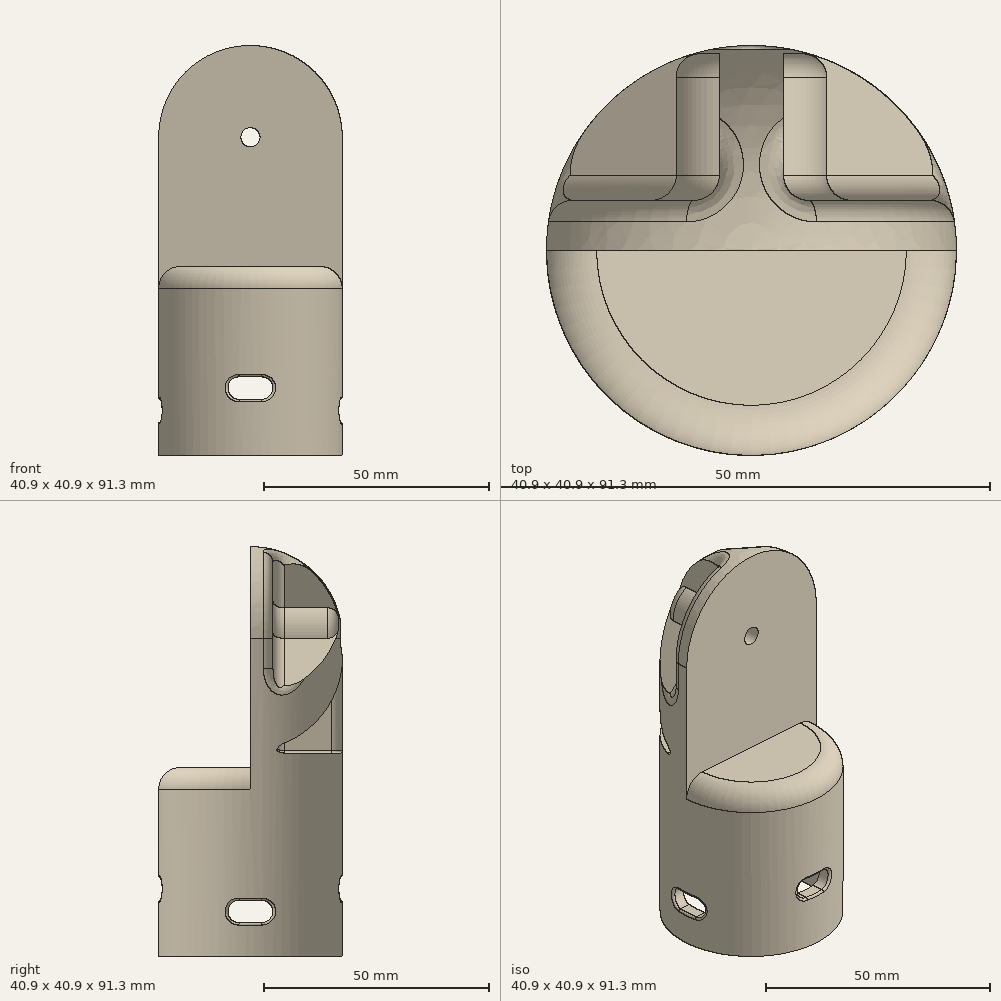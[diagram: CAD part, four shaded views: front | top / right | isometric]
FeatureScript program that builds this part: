
annotation { "Feature Type Name" : "Feature", "Feature Type Description" : "" }
export const myFeature = defineFeature(function(context is Context, id is Id, definition is map)
    precondition{}
    {
        {
            var Q0;
            Q0=qCreatedBy(makeId("Front.planeOp"),FACE);
            var sketch = newSketch(context, id + "F0", { "sketchPlane" : qUnion([Q0])});
            skLineSegment(sketch, "E0", {"start": v(17.25, 0) * mm, "end": v(17.25, 33.1) * mm});
            skLineSegment(sketch, "E1", {"start": v(12.25, 38.1) * mm, "end": v(0, 38.1) * mm});
            skLineSegment(sketch, "E2", {"start": v(0, 38.1) * mm, "end": v(0, 41.3) * mm});
            skLineSegment(sketch, "E3", {"start": v(0, 41.3) * mm, "end": v(20.45, 41.3) * mm, "construction": true});
            skLineSegment(sketch, "E4", {"start": v(20.45, 41.3) * mm, "end": v(20.45, 0) * mm});
            skLineSegment(sketch, "E5", {"start": v(20.45, 0) * mm, "end": v(17.25, 0) * mm});
            skPoint(sketch, "E6.visualSharp", {"position": v(17.25, 38.1) * mm});
            skArc(sketch, "E6.filletArc", {"start": v(17.25, 33.1) * mm, "mid": v(15.79, 36.64) * mm, "end": v(12.25, 38.1) * mm});
            skLineSegment(sketch, "E7", {"start": v(20.45, 41.3) * mm, "end": v(20.45, 70.85) * mm});
            skLineSegment(sketch, "E8", {"start": v(0, 91.3) * mm, "end": v(0, 91.3) * mm});
            skLineSegment(sketch, "E9", {"start": v(0, 91.3) * mm, "end": v(0, 41.3) * mm});
            skPoint(sketch, "E10.visualSharp", {"position": v(20.45, 91.3) * mm});
            skArc(sketch, "E10.filletArc", {"start": v(20.45, 70.85) * mm, "mid": v(14.46, 85.31) * mm, "end": v(0, 91.3) * mm});
            skSolve(sketch);
        }
        {
            var Q0;
            Q0=qSketchRegion(id+"F0",true);
            var Q1;
            Q1=sQuery(id+"F0.wireOp",EDGE,"E2");
            revolve(context, id + "F1", {"entities" : qUnion([Q0]), "axis" : qUnion([Q1]), "revolveType" : RevolveType.FULL});
        }
        {
            var Q0;
            Q0=qCreatedBy(makeId("Front.planeOp"),FACE);
            var sketch = newSketch(context, id + "F2", { "sketchPlane" : qUnion([Q0])});
            skArc(sketch, "E11", {"start": v(20.45, 70.85) * mm, "mid": v(0, 91.3) * mm, "end": v(-20.45, 70.85) * mm});
            skLineSegment(sketch, "E12", {"start": v(-20.45, 70.85) * mm, "end": v(-20.45, 42.1) * mm});
            skLineSegment(sketch, "E13", {"start": v(-20.45, 42.1) * mm, "end": v(20.45, 42.1) * mm});
            skLineSegment(sketch, "E14", {"start": v(20.45, 42.1) * mm, "end": v(20.45, 70.85) * mm});
            skSolve(sketch);
        }
        {
            var Q0;
            Q0=qSketchRegion(id+"F2",true);
            extrude(context, id + "F3", {"entities" : qUnion([Q0]), "operationType" : NewBodyOperationType.REMOVE, "depth" : 25 * mm});
        }
        {
            var Q0;
            Q0=qCreatedBy(makeId("Front.planeOp"),FACE);
            cPlane(context, id + "F4", {"entities" : qUnion([Q0]), "cplaneType" : CPlaneType.OFFSET, "offset" : 5 * mm, "oppositeDirection" : true, "width" : 150 * mm, "height" : 150 * mm});
        }
        {
            var Q0;
            Q0=makeQuery(id+"F3.boolean.opBoolean","INTERSECT",EDGE,{"derivedFrom":[makeQuery(id+"F1.opRevolve","SWEPT_FACE",FACE,{"disambiguationData":[OSD([sQuery(id+"F0.wireOp",EDGE,"E4"),sQuery(id+"F0.wireOp",EDGE,"E7")])]}),makeQuery(id+"F3.opExtrude","SWEPT_FACE",FACE,{"disambiguationData":[OSD([sQuery(id+"F2.wireOp",EDGE,"E13")])]})]});
            fillet(context, id + "F5", {"entities" : qUnion([Q0]), "radius" : 5 * mm, "tangentPropagation" : true, "allowEdgeOverflow" : false});
        }
        {
            var Q0;
            Q0=qCreatedBy(makeId("Front.planeOp"),FACE);
            var sketch = newSketch(context, id + "F6", { "sketchPlane" : qUnion([Q0])});
            skLineSegment(sketch, "E15.bottom", {"start": v(2.5, 12.5) * mm, "end": v(-2.5, 12.5) * mm});
            skLineSegment(sketch, "E15.top", {"start": v(2.5, 17.5) * mm, "end": v(-2.5, 17.5) * mm});
            skLineSegment(sketch, "E15.left", {"start": v(5, 15) * mm, "end": v(5, 15) * mm});
            skLineSegment(sketch, "E15.right", {"start": v(-5, 15) * mm, "end": v(-5, 15) * mm});
            skPoint(sketch, "E15.middle", {"position": v(0, 15) * mm});
            skPoint(sketch, "E16.visualSharp", {"position": v(-5, 17.5) * mm});
            skArc(sketch, "E16.filletArc", {"start": v(-2.5, 17.5) * mm, "mid": v(-4.27, 16.77) * mm, "end": v(-5, 15) * mm});
            skPoint(sketch, "E17.visualSharp", {"position": v(-5, 12.5) * mm});
            skArc(sketch, "E17.filletArc", {"start": v(-5, 15) * mm, "mid": v(-4.27, 13.23) * mm, "end": v(-2.5, 12.5) * mm});
            skPoint(sketch, "E18.visualSharp", {"position": v(5, 12.5) * mm});
            skArc(sketch, "E18.filletArc", {"start": v(2.5, 12.5) * mm, "mid": v(4.27, 13.23) * mm, "end": v(5, 15) * mm});
            skPoint(sketch, "E19.visualSharp", {"position": v(5, 17.5) * mm});
            skArc(sketch, "E19.filletArc", {"start": v(5, 15) * mm, "mid": v(4.27, 16.77) * mm, "end": v(2.5, 17.5) * mm});
            skSolve(sketch);
        }
        {
            var Q0;
            Q0=qSketchRegion(id+"F6",true);
            extrude(context, id + "F7", {"entities" : qUnion([Q0]), "operationType" : NewBodyOperationType.REMOVE, "endBound" : BoundingType.SYMMETRIC, "oppositeDirection" : true, "depth" : 60 * mm});
        }
        {
            var Q0;
            Q0=qCreatedBy(makeId("Right.planeOp"),FACE);
            var sketch = newSketch(context, id + "F8", { "sketchPlane" : qUnion([Q0])});
            skLineSegment(sketch, "E20.bottom", {"start": v(2.5, 7.5) * mm, "end": v(-2.5, 7.5) * mm});
            skLineSegment(sketch, "E20.top", {"start": v(2.5, 12.5) * mm, "end": v(-2.5, 12.5) * mm});
            skLineSegment(sketch, "E20.left", {"start": v(5, 10) * mm, "end": v(5, 10) * mm});
            skLineSegment(sketch, "E20.right", {"start": v(-5, 10) * mm, "end": v(-5, 10) * mm});
            skPoint(sketch, "E20.middle", {"position": v(0, 10) * mm});
            skPoint(sketch, "E21.visualSharp", {"position": v(-5, 12.5) * mm});
            skArc(sketch, "E21.filletArc", {"start": v(-2.5, 12.5) * mm, "mid": v(-4.27, 11.77) * mm, "end": v(-5, 10) * mm});
            skPoint(sketch, "E22.visualSharp", {"position": v(5, 12.5) * mm});
            skArc(sketch, "E22.filletArc", {"start": v(5, 10) * mm, "mid": v(4.27, 11.77) * mm, "end": v(2.5, 12.5) * mm});
            skPoint(sketch, "E23.visualSharp", {"position": v(5, 7.5) * mm});
            skArc(sketch, "E23.filletArc", {"start": v(2.5, 7.5) * mm, "mid": v(4.27, 8.23) * mm, "end": v(5, 10) * mm});
            skPoint(sketch, "E24.visualSharp", {"position": v(-5, 7.5) * mm});
            skArc(sketch, "E24.filletArc", {"start": v(-5, 10) * mm, "mid": v(-4.27, 8.23) * mm, "end": v(-2.5, 7.5) * mm});
            skSolve(sketch);
        }
        {
            var Q0;
            Q0=qSketchRegion(id+"F8",true);
            extrude(context, id + "F9", {"entities" : qUnion([Q0]), "operationType" : NewBodyOperationType.REMOVE, "endBound" : BoundingType.SYMMETRIC, "depth" : 60 * mm});
        }
        {
            var Q0;
            Q0=qCreatedBy(id+"F4.planeOp",FACE);
            var sketch = newSketch(context, id + "F10", { "sketchPlane" : qUnion([Q0])});
            skArc(sketch, "E25", {"start": v(-20.45, 70.85) * mm, "mid": v(-15.55, 84.13) * mm, "end": v(-3.2, 91.05) * mm});
            skLineSegment(sketch, "E26", {"start": v(20.45, 70.85) * mm, "end": v(20.45, 57.9) * mm});
            skLineSegment(sketch, "E27", {"start": v(20.45, 45.3) * mm, "end": v(-20.45, 45.3) * mm});
            skLineSegment(sketch, "E28", {"start": v(-20.45, 57.9) * mm, "end": v(-20.45, 70.85) * mm});
            skArc(sketch, "E29", {"start": v(7.5, 70.85) * mm, "mid": v(6.33, 74.87) * mm, "end": v(3.2, 77.63) * mm});
            skLineSegment(sketch, "E30.bottom", {"start": v(3.2, 45.3) * mm, "end": v(-3.2, 45.3) * mm});
            skLineSegment(sketch, "E30.left", {"start": v(3.2, 45.3) * mm, "end": v(3.2, 63.3) * mm});
            skLineSegment(sketch, "E30.right", {"start": v(-3.2, 45.3) * mm, "end": v(-3.2, 63.3) * mm});
            skLineSegment(sketch, "E31", {"start": v(-20.45, 57.9) * mm, "end": v(-7.5, 70.85) * mm});
            skLineSegment(sketch, "E32", {"start": v(20.45, 57.9) * mm, "end": v(7.5, 70.85) * mm});
            skLineSegment(sketch, "E33", {"start": v(3.2, 77.63) * mm, "end": v(3.2, 91.05) * mm});
            skLineSegment(sketch, "E34", {"start": v(-3.2, 77.63) * mm, "end": v(-3.2, 91.05) * mm});
            skArc(sketch, "E35.trimOffspring", {"start": v(-3.2, 77.63) * mm, "mid": v(-6.33, 74.87) * mm, "end": v(-7.5, 70.85) * mm});
            skArc(sketch, "E36.trimOffspring", {"start": v(3.2, 91.05) * mm, "mid": v(15.55, 84.13) * mm, "end": v(20.45, 70.85) * mm});
            skLineSegment(sketch, "E37", {"start": v(20.45, 45.3) * mm, "end": v(20.45, 46.05) * mm});
            skLineSegment(sketch, "E38", {"start": v(20.45, 46.05) * mm, "end": v(3.2, 63.3) * mm});
            skLineSegment(sketch, "E39", {"start": v(-20.45, 45.3) * mm, "end": v(-20.45, 46.05) * mm});
            skLineSegment(sketch, "E40", {"start": v(-20.45, 46.05) * mm, "end": v(-3.2, 63.3) * mm});
            skCircle(sketch, "E41", {"center": v(0, 70.85) * mm, "radius": 3.5 * mm});
            skSolve(sketch);
        }
        {
            var Q0;
            Q0=qSketchRegion(id+"F10",true);
            extrude(context, id + "F11", {"entities" : qUnion([Q0]), "operationType" : NewBodyOperationType.REMOVE, "oppositeDirection" : true, "depth" : 25 * mm});
        }
        {
            var Q0;
            Q0=makeQuery(id+"F3.boolean.opBoolean","COPY",FACE,{"derivedFrom":makeQuery(id+"F3.opExtrude","CAP_FACE",FACE,{"disambiguationData":[OSD([sQuery(id+"F2.wireOp",EDGE,"E11"),sQuery(id+"F2.wireOp",EDGE,"E12"),sQuery(id+"F2.wireOp",EDGE,"E13"),sQuery(id+"F2.wireOp",EDGE,"E14")])],"isStart":true})});
            var sketch = newSketch(context, id + "F12", { "sketchPlane" : qUnion([Q0])});
            skCircle(sketch, "E42", {"center": v(0, 70.85) * mm, "radius": 2.12 * mm});
            skSolve(sketch);
        }
        {
            var Q0;
            Q0=qSketchRegion(id+"F12",true);
            extrude(context, id + "F13", {"entities" : qUnion([Q0]), "operationType" : NewBodyOperationType.REMOVE, "endBound" : BoundingType.THROUGH_ALL, "oppositeDirection" : true, "depth" : 25 * mm});
        }
        {
            var Q0;
            Q0=makeQuery(id+"F11.boolean.opBoolean","COPY",FACE,{"derivedFrom":makeQuery(id+"F11.opExtrude","CAP_FACE",FACE,{"disambiguationData":[OSD([sQuery(id+"F10.wireOp",EDGE,"E26"),sQuery(id+"F10.wireOp",EDGE,"E29"),sQuery(id+"F10.wireOp",EDGE,"E32"),sQuery(id+"F10.wireOp",EDGE,"E33"),sQuery(id+"F10.wireOp",EDGE,"E36.trimOffspring")])],"isStart":true})});
            var Q1;
            Q1=makeQuery(id+"F11.boolean.opBoolean","COPY",FACE,{"derivedFrom":makeQuery(id+"F11.opExtrude","CAP_FACE",FACE,{"disambiguationData":[OSD([sQuery(id+"F10.wireOp",EDGE,"E25"),sQuery(id+"F10.wireOp",EDGE,"E28"),sQuery(id+"F10.wireOp",EDGE,"E31"),sQuery(id+"F10.wireOp",EDGE,"E34"),sQuery(id+"F10.wireOp",EDGE,"E35.trimOffspring")])],"isStart":true})});
            var Q2;
            Q2=makeQuery(id+"F11.boolean.opBoolean","COPY",FACE,{"derivedFrom":makeQuery(id+"F11.opExtrude","CAP_FACE",FACE,{"disambiguationData":[OSD([sQuery(id+"F10.wireOp",EDGE,"E27"),sQuery(id+"F10.wireOp",EDGE,"E30.right"),sQuery(id+"F10.wireOp",EDGE,"E39"),sQuery(id+"F10.wireOp",EDGE,"E40")])],"isStart":true})});
            var Q3;
            Q3=makeQuery(id+"F11.boolean.opBoolean","COPY",FACE,{"derivedFrom":makeQuery(id+"F11.opExtrude","CAP_FACE",FACE,{"disambiguationData":[OSD([sQuery(id+"F10.wireOp",EDGE,"E27"),sQuery(id+"F10.wireOp",EDGE,"E30.left"),sQuery(id+"F10.wireOp",EDGE,"E37"),sQuery(id+"F10.wireOp",EDGE,"E38")])],"isStart":true})});
            var Q4;
            Q4=makeQuery(id+"F11.boolean.opBoolean","INTERSECT",EDGE,{"derivedFrom":[makeQuery(id+"F1.opRevolve","SWEPT_FACE",FACE,{"disambiguationData":[OSD([sQuery(id+"F0.wireOp",EDGE,"E10.filletArc")])]}),makeQuery(id+"F11.opExtrude","SWEPT_FACE",FACE,{"disambiguationData":[OSD([sQuery(id+"F10.wireOp",EDGE,"E29")])]})]});
            var Q5;
            Q5=makeQuery(id+"F11.boolean.opBoolean","INTERSECT",EDGE,{"derivedFrom":[makeQuery(id+"F1.opRevolve","SWEPT_FACE",FACE,{"disambiguationData":[OSD([sQuery(id+"F0.wireOp",EDGE,"E10.filletArc")])]}),makeQuery(id+"F11.opExtrude","SWEPT_FACE",FACE,{"disambiguationData":[OSD([sQuery(id+"F10.wireOp",EDGE,"E35.trimOffspring")])]})]});
            var Q6;
            Q6=makeQuery(id+"F11.boolean.opBoolean","INTERSECT",EDGE,{"derivedFrom":[makeQuery(id+"F1.opRevolve","SWEPT_FACE",FACE,{"disambiguationData":[OSD([sQuery(id+"F0.wireOp",EDGE,"E4"),sQuery(id+"F0.wireOp",EDGE,"E7")])]}),makeQuery(id+"F11.opExtrude","SWEPT_FACE",FACE,{"disambiguationData":[OSD([sQuery(id+"F10.wireOp",EDGE,"E30.right")])]})]});
            var Q7;
            Q7=makeQuery(id+"F11.boolean.opBoolean","INTERSECT",EDGE,{"derivedFrom":[makeQuery(id+"F1.opRevolve","SWEPT_FACE",FACE,{"disambiguationData":[OSD([sQuery(id+"F0.wireOp",EDGE,"E4"),sQuery(id+"F0.wireOp",EDGE,"E7")])]}),makeQuery(id+"F11.opExtrude","SWEPT_FACE",FACE,{"disambiguationData":[OSD([sQuery(id+"F10.wireOp",EDGE,"E30.left")])]})]});
            fillet(context, id + "F14", {"entities" : qUnion([Q0, Q1, Q2, Q3, Q4, Q5, Q6, Q7]), "radius" : 2.5 * mm, "tangentPropagation" : true, "allowEdgeOverflow" : false});
        }
        {
            var Q0;
            Q0=makeQuery(id+"F11.boolean.opBoolean","INTERSECT",EDGE,{"derivedFrom":[makeQuery(id+"F1.opRevolve","SWEPT_FACE",FACE,{"disambiguationData":[OSD([sQuery(id+"F0.wireOp",EDGE,"E10.filletArc")])]}),makeQuery(id+"F11.opExtrude","SWEPT_FACE",FACE,{"disambiguationData":[OSD([sQuery(id+"F10.wireOp",EDGE,"E41")])]})]});
            var Q1;
            Q1=makeQuery(id+"F11.boolean.opBoolean","INTERSECT",EDGE,{"derivedFrom":[makeQuery(id+"F1.opRevolve","SWEPT_FACE",FACE,{"disambiguationData":[OSD([sQuery(id+"F0.wireOp",EDGE,"E4"),sQuery(id+"F0.wireOp",EDGE,"E7")])]}),makeQuery(id+"F11.opExtrude","SWEPT_FACE",FACE,{"disambiguationData":[OSD([sQuery(id+"F10.wireOp",EDGE,"E41")])]})]});
            var Q2;
            Q2=makeQuery(id+"F7.boolean.opBoolean","INTERSECT",EDGE,{"disambiguationData":[OD(1.0)],"derivedFrom":[makeQuery(id+"F1.opRevolve","SWEPT_FACE",FACE,{"disambiguationData":[OSD([sQuery(id+"F0.wireOp",EDGE,"E4"),sQuery(id+"F0.wireOp",EDGE,"E7")])]}),makeQuery(id+"F7.opExtrude","SWEPT_FACE",FACE,{"disambiguationData":[OSD([sQuery(id+"F6.wireOp",EDGE,"E16.filletArc"),sQuery(id+"F6.wireOp",EDGE,"E17.filletArc")])]})]});
            var Q3;
            Q3=makeQuery(id+"F9.boolean.opBoolean","INTERSECT",EDGE,{"disambiguationData":[OD(1.0)],"derivedFrom":[makeQuery(id+"F1.opRevolve","SWEPT_FACE",FACE,{"disambiguationData":[OSD([sQuery(id+"F0.wireOp",EDGE,"E4"),sQuery(id+"F0.wireOp",EDGE,"E7")])]}),makeQuery(id+"F9.opExtrude","SWEPT_FACE",FACE,{"disambiguationData":[OSD([sQuery(id+"F8.wireOp",EDGE,"E22.filletArc"),sQuery(id+"F8.wireOp",EDGE,"E23.filletArc")])]})]});
            var Q4;
            Q4=makeQuery(id+"F7.boolean.opBoolean","INTERSECT",EDGE,{"disambiguationData":[OD(0.0)],"derivedFrom":[makeQuery(id+"F1.opRevolve","SWEPT_FACE",FACE,{"disambiguationData":[OSD([sQuery(id+"F0.wireOp",EDGE,"E4"),sQuery(id+"F0.wireOp",EDGE,"E7")])]}),makeQuery(id+"F7.opExtrude","SWEPT_FACE",FACE,{"disambiguationData":[OSD([sQuery(id+"F6.wireOp",EDGE,"E18.filletArc"),sQuery(id+"F6.wireOp",EDGE,"E19.filletArc")])]})]});
            var Q5;
            Q5=makeQuery(id+"F9.boolean.opBoolean","INTERSECT",EDGE,{"disambiguationData":[OD(0.0)],"derivedFrom":[makeQuery(id+"F1.opRevolve","SWEPT_FACE",FACE,{"disambiguationData":[OSD([sQuery(id+"F0.wireOp",EDGE,"E4"),sQuery(id+"F0.wireOp",EDGE,"E7")])]}),makeQuery(id+"F9.opExtrude","SWEPT_FACE",FACE,{"disambiguationData":[OSD([sQuery(id+"F8.wireOp",EDGE,"E21.filletArc"),sQuery(id+"F8.wireOp",EDGE,"E24.filletArc")])]})]});
            var Q6;
            Q6=makeQuery(id+"F11.boolean.opBoolean","COPY",EDGE,{"derivedFrom":makeQuery(id+"F11.opExtrude","SWEPT_EDGE",EDGE,{"disambiguationData":[OSD([sQuery(id+"F10.wireOp",EDGE,"E30.right"),sQuery(id+"F10.wireOp",EDGE,"SenA7yMq-X0Jc-aKfk-Isei-V5cgANuGZ9FP")])]})});
            var Q7;
            Q7=makeQuery(id+"F11.boolean.opBoolean","COPY",EDGE,{"derivedFrom":makeQuery(id+"F11.opExtrude","SWEPT_EDGE",EDGE,{"disambiguationData":[OSD([sQuery(id+"F10.wireOp",EDGE,"E30.left"),sQuery(id+"F10.wireOp",EDGE,"qmb3wQXh-fVJP-rPFq-4pph-YRSkXsj6tfTi")])]})});
            var Q8;
            Q8=makeQuery(id+"F11.boolean.opBoolean","COPY",EDGE,{"derivedFrom":makeQuery(id+"F11.opExtrude","SWEPT_EDGE",EDGE,{"disambiguationData":[OSD([sQuery(id+"F10.wireOp",EDGE,"E38"),sQuery(id+"F10.wireOp",EDGE,"qmb3wQXh-fVJP-rPFq-4pph-YRSkXsj6tfTi")])]})});
            var Q9;
            Q9=makeQuery(id+"F11.boolean.opBoolean","COPY",EDGE,{"derivedFrom":makeQuery(id+"F11.opExtrude","SWEPT_EDGE",EDGE,{"disambiguationData":[OSD([sQuery(id+"F10.wireOp",EDGE,"E40"),sQuery(id+"F10.wireOp",EDGE,"SenA7yMq-X0Jc-aKfk-Isei-V5cgANuGZ9FP")])]})});
            fillet(context, id + "F15", {"entities" : qUnion([Q0, Q1, Q2, Q3, Q4, Q5, Q6, Q7, Q8, Q9]), "radius" : .5 * mm, "tangentPropagation" : true, "allowEdgeOverflow" : false});
        }
        {
            var Q0;
            Q0=makeQuery(id+"F11.boolean.opBoolean","COPY",FACE,{"derivedFrom":makeQuery(id+"F11.opExtrude","CAP_FACE",FACE,{"disambiguationData":[OSD([sQuery(id+"F10.wireOp",EDGE,"E41")])],"isStart":true})});
            var sketch = newSketch(context, id + "F16", { "sketchPlane" : qUnion([Q0])});
            skCircle(sketch, "E43.cCircle", {"center": v(0, 70.85) * mm, "radius": 2.93 * mm, "construction": true});
            skLineSegment(sketch, "E43.0", {"start": v(2.93, 72.54) * mm, "end": v(2.93, 69.16) * mm});
            skLineSegment(sketch, "E43.1", {"start": v(2.92, 69.16) * mm, "end": v(0, 67.47) * mm});
            skLineSegment(sketch, "E43.2", {"start": v(0, 67.47) * mm, "end": v(-2.92, 69.16) * mm});
            skLineSegment(sketch, "E43.3", {"start": v(-2.93, 69.16) * mm, "end": v(-2.93, 72.54) * mm});
            skLineSegment(sketch, "E43.4", {"start": v(-2.93, 72.54) * mm, "end": v(0, 74.23) * mm});
            skLineSegment(sketch, "E43.5", {"start": v(0, 74.23) * mm, "end": v(2.93, 72.54) * mm});
            skPoint(sketch, "E43.0.midPoint", {"position": v(2.93, 70.85) * mm});
            skCircle(sketch, "E44", {"center": v(0, 70.85) * mm, "radius": 3.5 * mm});
            skSolve(sketch);
        }
        {
            var Q0;
            Q0 = qSketchRegion(id + "F16", true);
            extrude(context, id + "F17", {"entities" : qUnion([Q0]), "operationType" : NewBodyOperationType.ADD, "depth" : 4 * mm});
        }
    });
